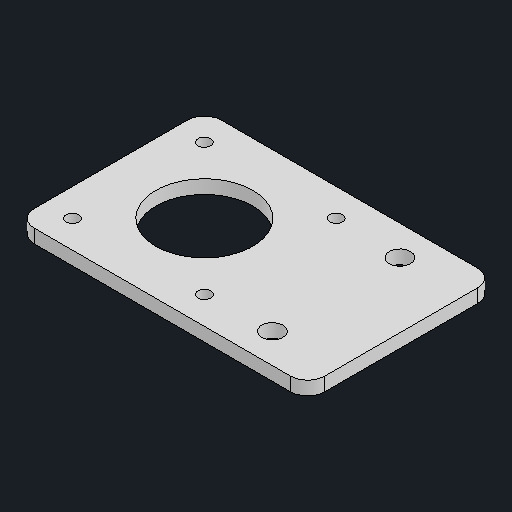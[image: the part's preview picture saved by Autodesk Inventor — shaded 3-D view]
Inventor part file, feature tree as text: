
AUTODESK INVENTOR PART (.ipt)
format: ipt  version: 2024.2 (Build 282272000, 272)  size: 92,672 bytes
history: native  units: mm
features: other x1, fillet x1
ambient origin geometry x8: Origin, YZ Plane, XZ Plane, XY Plane, X Axis, Y Axis, Z Axis, Center Point
bodies: Body1 (feature_tree)
feature tree (2):
  other  "솔리드1"
  fillet  "Fillet1"  [1 undecoded]
note: 1 required parameter value undecoded (feature->parameter linkage not recoverable at this tier; creation-order binding heuristic only, values carry confidence <= 0.55)
